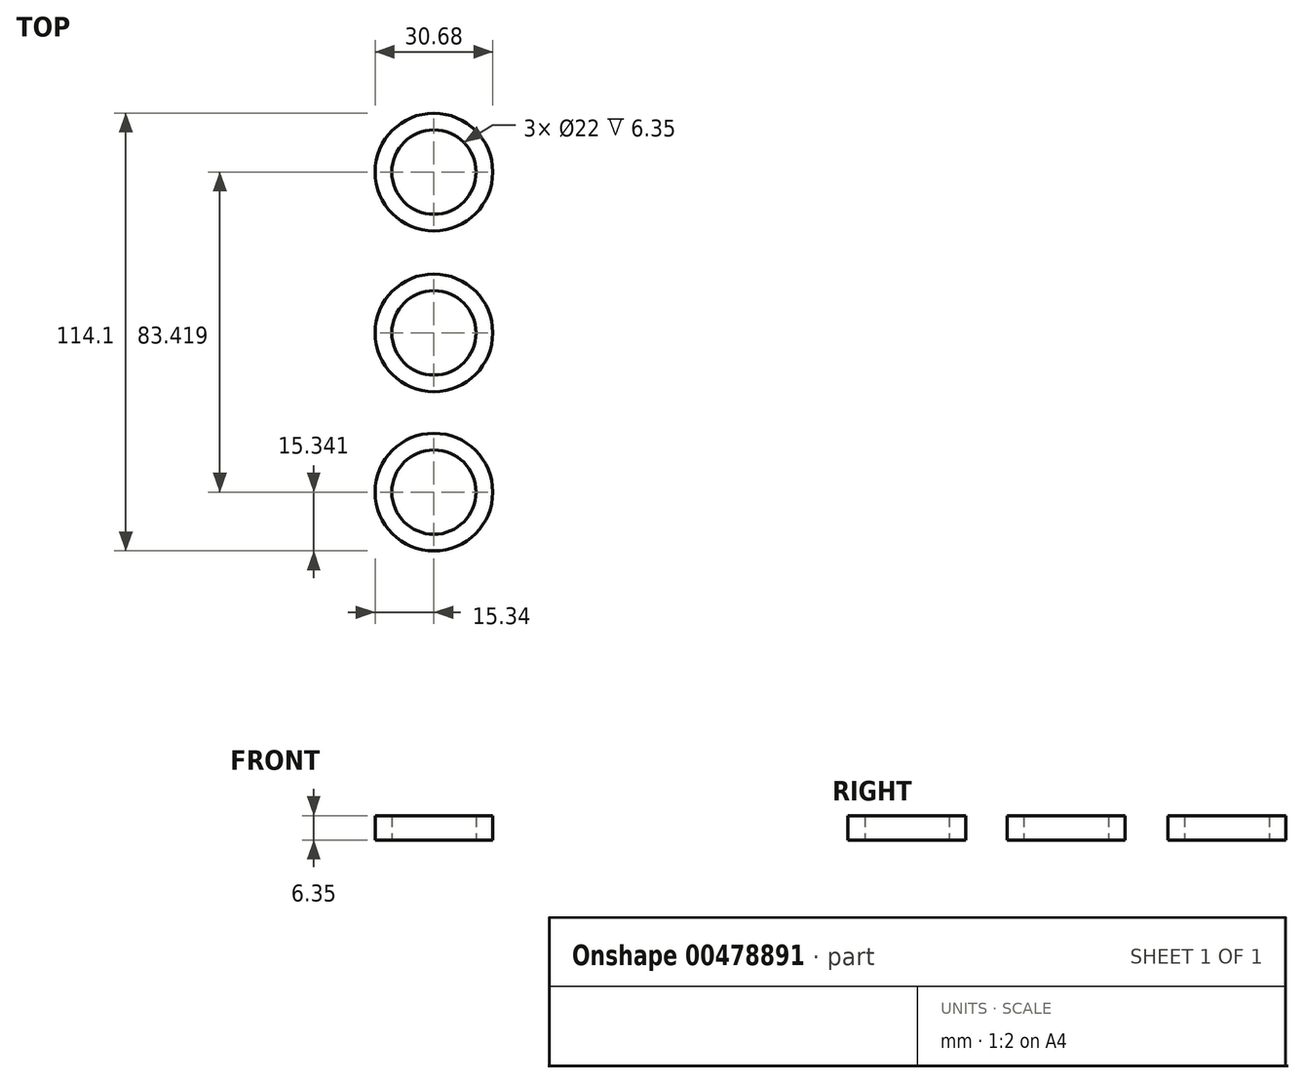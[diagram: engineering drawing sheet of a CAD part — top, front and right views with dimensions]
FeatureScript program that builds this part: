
annotation { "Feature Type Name" : "Feature", "Feature Type Description" : "" }
export const myFeature = defineFeature(function(context is Context, id is Id, definition is map)
    precondition{}
    {
        {
            var Q0;
            Q0=qCreatedBy(makeId("Top.planeOp"),FACE);
            var sketch = newSketch(context, id + "F0", { "sketchPlane" : qUnion([Q0])});
            skCircle(sketch, "E0", {"center": v(0, 0) * mm, "radius": 11 * mm});
            skSolve(sketch);
        }
        {
            var Q0;
            Q0=makeQuery(id+"F0.imprint","IMPRINT",FACE,{"disambiguationData":[TD([[makeQuery(id+"F0.imprint","IMPRINT",EDGE,{"derivedFrom":sQuery(id+"F0.wireOp",EDGE,"E0")}),1.0]])]});
            var sketch = newSketch(context, id + "F1", { "sketchPlane" : qUnion([Q0])});
            skCircle(sketch, "E1", {"center": v(0, 0) * mm, "radius": 15.34 * mm});
            skSolve(sketch);
        }
        {
            var Q0;
            Q0=qCreatedBy(makeId("Top.planeOp"),FACE);
            var sketch = newSketch(context, id + "F2", { "sketchPlane" : qUnion([Q0])});
            skCircle(sketch, "E2", {"center": v(0, 41.91) * mm, "radius": 15.34 * mm});
            skCircle(sketch, "E3", {"center": v(0, 41.91) * mm, "radius": 11 * mm});
            skCircle(sketch, "E4", {"center": v(0, -41.5) * mm, "radius": 15.34 * mm});
            skCircle(sketch, "E5", {"center": v(0, -41.5) * mm, "radius": 11 * mm});
            skSolve(sketch);
        }
        {
            var Q0;
            Q0=makeQuery(id+"F1.imprint","IMPRINT",FACE,{"disambiguationData":[TD([[makeQuery(id+"F1.imprint","IMPRINT",EDGE,{"derivedFrom":sQuery(id+"F1.wireOp",EDGE,"E1")}),1.0]])]});
            var Q1;
            Q1=makeQuery(id+"F2.imprint","IMPRINT",FACE,{"disambiguationData":[TD([[makeQuery(id+"F2.imprint","IMPRINT",EDGE,{"derivedFrom":sQuery(id+"F2.wireOp",EDGE,"E2")}),1.0]])]});
            var Q2;
            Q2=makeQuery(id+"F2.imprint","IMPRINT",FACE,{"disambiguationData":[TD([[makeQuery(id+"F2.imprint","IMPRINT",EDGE,{"derivedFrom":sQuery(id+"F2.wireOp",EDGE,"E4")}),1.0]])]});
            extrude(context, id + "F3", {"entities" : qUnion([Q0, Q1, Q2]), "depth" : 6.35 * mm});
        }
    });
